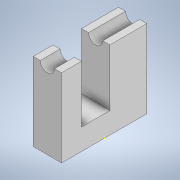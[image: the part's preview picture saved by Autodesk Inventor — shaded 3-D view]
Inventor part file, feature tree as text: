
AUTODESK INVENTOR PART (.ipt)
format: ipt  version: 2021 (Build 250183000, 183)  size: 329,216 bytes
history: native  units: mm
features: sketch x6, extrude x4, emboss x1
ambient origin geometry x8: Origin, YZ Plane, XZ Plane, XY Plane, X Axis, Y Axis, Z Axis, Center Point
bodies: Solid1 (feature_tree)
feature tree (11):
  extrude  "Extrusion1"  Depth=10.0mm
  sketch  "Sketch4"  dims[d2=5.0mm d3=15.0mm]
  extrude  "Extrusion4"  Depth=15.0mm
  extrude  "Extrusion5"  Depth=7.0mm
  extrude  "Extrusion6"  Depth=20.0mm
  emboss  "Emboss1"
  sketch  "Sketch1"  dims[d0=30.0mm d1=10.0mm]
  sketch  "Sketch5"  dims[d4=27.5mm d5=0.0mm d12=7.0mm]
  sketch  "Sketch6"  dims[d14=10.0mm d15=20.0mm]
  sketch  "Sketch8"  dims[d16=0.0mm d17=0.0mm]
  sketch  "Sketch9"  dims[d18=5.0mm d19=0.0mm d20=0.0mm d24=3.0mm d26=3.0mm d27=0.0mm d28=19.0mm d29=1.0mm d30=0.0mm]
